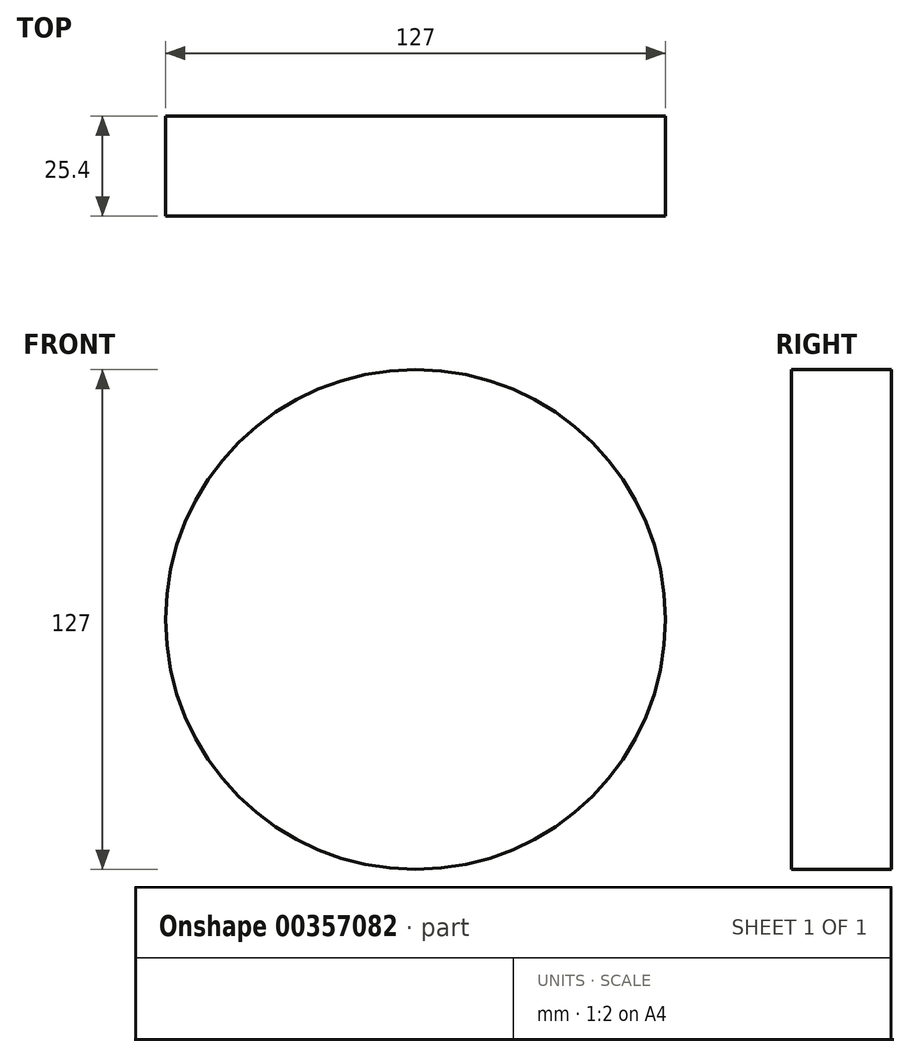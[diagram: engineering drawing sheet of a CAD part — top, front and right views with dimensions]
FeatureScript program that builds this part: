
annotation { "Feature Type Name" : "Feature", "Feature Type Description" : "" }
export const myFeature = defineFeature(function(context is Context, id is Id, definition is map)
    precondition{}
    {
        {
            var Q0;
            Q0=qCreatedBy(makeId("Front.planeOp"),FACE);
            var sketch = newSketch(context, id + "F0", { "sketchPlane" : qUnion([Q0])});
            skCircle(sketch, "E0", {"center": v(0, 0) * mm, "radius": 57.15 * mm});
            skCircle(sketch, "E1", {"center": v(3.17, 0) * mm, "radius": 57.15 * mm});
            skLineSegment(sketch, "E2", {"start": v(57.15, 0) * mm, "end": v(60.33, 0) * mm});
            skLineSegment(sketch, "E3", {"start": v(-57.15, 0) * mm, "end": v(-53.98, 0) * mm});
            skCircle(sketch, "E4", {"center": v(0, 0) * mm, "radius": 63.5 * mm});
            skSolve(sketch);
        }
        {
            var Q0;
            {var subQ0=sQuery(id+"F0.wireOp",EDGE,"E0");var subQ1=makeQuery(id+"F0.imprint","INTERSECT",VERTEX,{"derivedFrom":[subQ0,sQuery(id+"F0.wireOp",EDGE,"E2")]});Q0=makeQuery(id+"F0.imprint","IMPRINT",FACE,{"disambiguationData":[TD([[makeQuery(id+"F0.imprint","IMPRINT",EDGE,{"disambiguationData":[TD([[subQ1,-1.0]])],"derivedFrom":subQ0}),1.0]])]});}
            var Q1;
            {var subQ0=sQuery(id+"F0.wireOp",EDGE,"E3");Q1=makeQuery(id+"F0.imprint","IMPRINT",FACE,{"disambiguationData":[TD([[makeQuery(id+"F0.imprint","IMPRINT",EDGE,{"derivedFrom":subQ0}),1.0]])]});}
            var Q2;
            {var subQ0=sQuery(id+"F0.wireOp",EDGE,"E3");Q2=makeQuery(id+"F0.imprint","IMPRINT",FACE,{"disambiguationData":[TD([[makeQuery(id+"F0.imprint","IMPRINT",EDGE,{"derivedFrom":subQ0}),-1.0]])]});}
            var Q3;
            {var subQ0=sQuery(id+"F0.wireOp",EDGE,"E2");Q3=makeQuery(id+"F0.imprint","IMPRINT",FACE,{"disambiguationData":[TD([[makeQuery(id+"F0.imprint","IMPRINT",EDGE,{"derivedFrom":subQ0}),1.0]])]});}
            var Q4;
            {var subQ0=sQuery(id+"F0.wireOp",EDGE,"E2");Q4=makeQuery(id+"F0.imprint","IMPRINT",FACE,{"disambiguationData":[TD([[makeQuery(id+"F0.imprint","IMPRINT",EDGE,{"derivedFrom":subQ0}),-1.0]])]});}
            var Q5;
            Q5=makeQuery(id+"F0.imprint","IMPRINT",FACE,{"disambiguationData":[TD([[makeQuery(id+"F0.imprint","IMPRINT",EDGE,{"derivedFrom":sQuery(id+"F0.wireOp",EDGE,"E4")}),1.0]])]});
            extrude(context, id + "F1", {"entities" : qUnion([Q0, Q1, Q2, Q3, Q4, Q5]), "depth" : 25.4 * mm});
        }
    });
